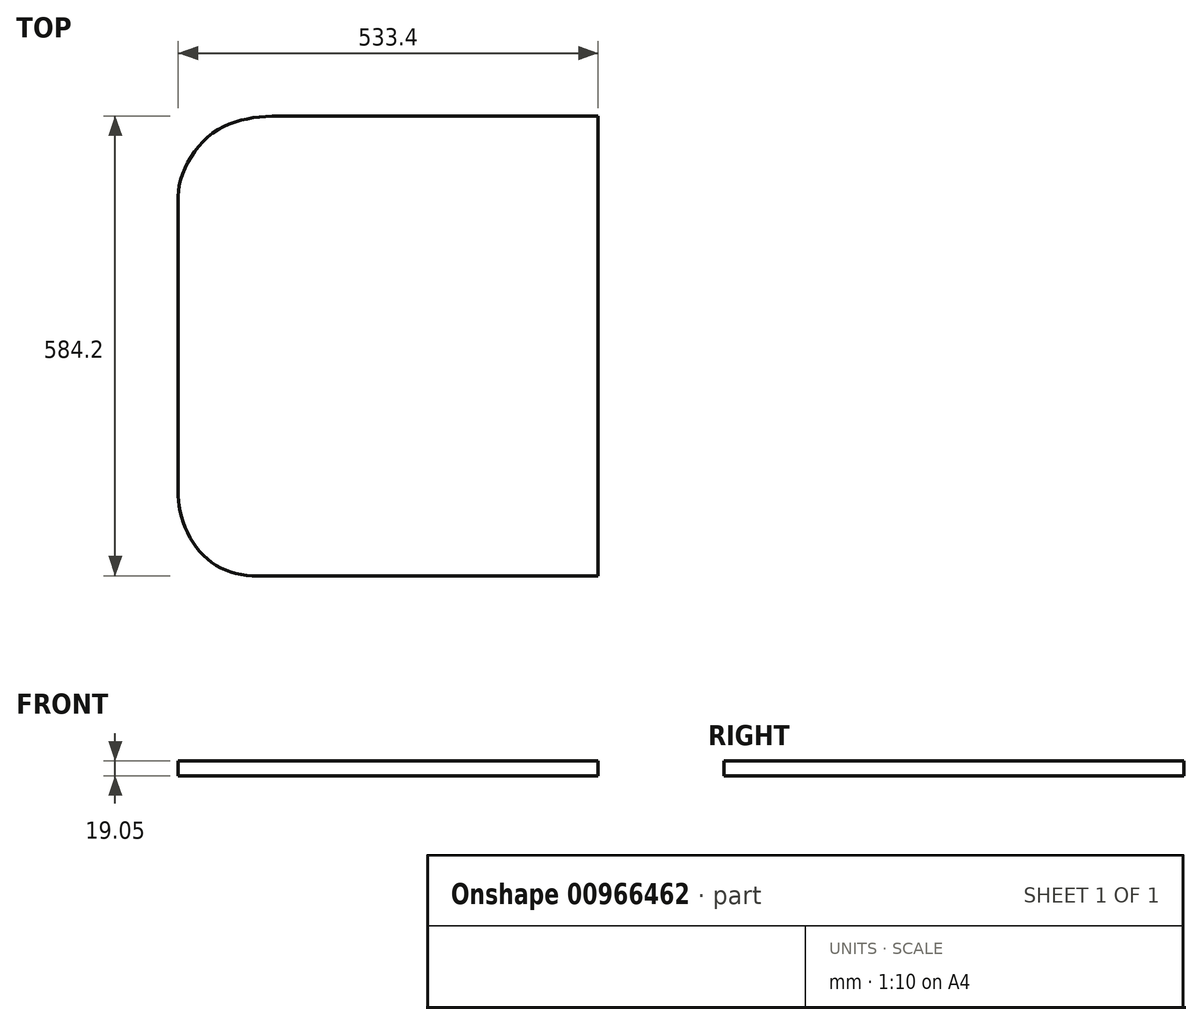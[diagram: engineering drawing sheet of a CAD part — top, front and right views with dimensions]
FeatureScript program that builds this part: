
annotation { "Feature Type Name" : "Feature", "Feature Type Description" : "" }
export const myFeature = defineFeature(function(context is Context, id is Id, definition is map)
    precondition{}
    {
        {
            var Q0;
            Q0=qCreatedBy(makeId("Top.planeOp"),FACE);
            var sketch = newSketch(context, id + "F0", { "sketchPlane" : qUnion([Q0])});
            skLineSegment(sketch, "E0.bottom", {"start": v(266.7, -292.1) * mm, "end": v(-165.1, -292.1) * mm});
            skLineSegment(sketch, "E0.top", {"start": v(266.7, 292.1) * mm, "end": v(-139.7, 292.1) * mm});
            skLineSegment(sketch, "E0.left", {"start": v(266.7, -292.1) * mm, "end": v(266.7, 292.1) * mm});
            skLineSegment(sketch, "E0.right", {"start": v(-266.7, -190.5) * mm, "end": v(-266.7, 190.5) * mm});
            skPoint(sketch, "E0.middle", {"position": v(0, 0) * mm});
            skFitSpline(sketch, "E1", {"points": [v(-266.7, -190.5) * mm, v(-236.4, -264.31) * mm, v(-165.1, -292.1) * mm], "startDerivative": vector(0, -145.97) * mm, "endDerivative": vector(175, 0) * mm});
            skFitSpline(sketch, "E2", {"points": [v(-139.7, 292.1) * mm, v(-227.23, 267.09) * mm, v(-266.7, 190.5) * mm], "startDerivative": vector(-180.23, 0) * mm, "endDerivative": vector(0, -146.73) * mm});
            skPoint(sketch, "E3.orphan", {"position": v(-266.7, 292.1) * mm});
            skPoint(sketch, "E4.orphan", {"position": v(-266.7, -292.1) * mm});
            skSolve(sketch);
        }
        {
            var Q0;
            Q0 = qSketchRegion(id + "F0", true);
            extrude(context, id + "F1", {"entities" : qUnion([Q0]), "depth" : 19.05 * mm, "offsetDistance" : 25.4 * mm});
        }
    });
